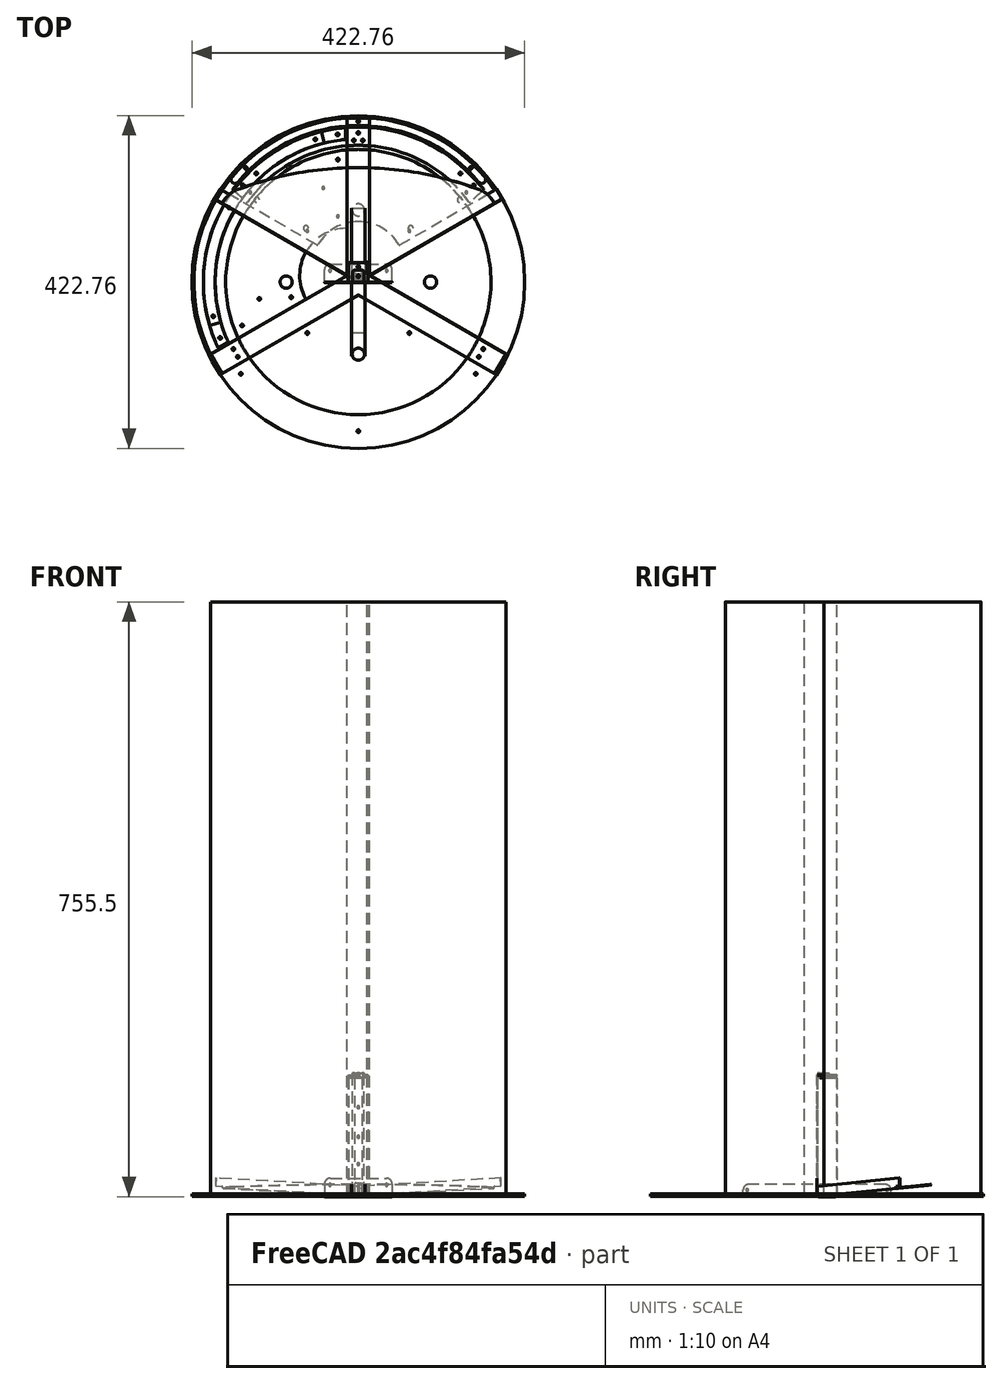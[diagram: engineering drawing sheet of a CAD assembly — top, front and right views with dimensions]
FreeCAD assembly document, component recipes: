
FREECAD ASSEMBLY — COMPONENT RECIPES ("composit_stand3-small")

This assembly document has 17 components, labeled P0..P16 below (a component is one placed body or linked part). 17 of them carry a construction recipe — the FreeCAD feature program that regenerates the part from scratch, quoted from this document or its linked companion documents; the rest are supplied as boundary geometry only. No exploded tour is included for this assembly.
NOTE — document 2 of 2 of this assembly tour. The two overview renders and the header above are repeated from document 1; the component sections below continue where the previous document stopped.
COMPONENT P16 — recipe-attached ("tech_pillar_material_0.50ansi", modeled in this document).
Construction recipe (the document's own serialized feature program — sketch geometry with constraints, then the solid features built on it; lengths are millimeters unless a unit is written):

FEATURE [PartDesign::CoordinateSystem] LCS_0006
  AttacherType = Attacher::AttachEngine3D
  MapMode = 2
  Support = -> [X_Axis037]
FEATURE [Sketcher::SketchObject] Sketch116
  FullyConstrained = true
  MapMode = 5
  Placement = pos=(0,0,0) rot=(0.57735,0.57735,0.57735;2.0944rad)
  Support = -> [YZ_Plane037]
  sketch-geometry (4):
    g0: LineSegment StartX=0 StartY=0 StartZ=0 EndX=25 EndY=0 EndZ=0
    g1: LineSegment StartX=25 StartY=0 StartZ=0 EndX=25 EndY=154 EndZ=0
    g2: LineSegment StartX=25 StartY=154 StartZ=0 EndX=0 EndY=154 EndZ=0
    g3: LineSegment StartX=0 StartY=154 StartZ=0 EndX=0 EndY=0 EndZ=0
  constraints (11):
    c: Coincident(g0,g1)
    c: Coincident(g1,g2)
    c: Coincident(g2,g3)
    c: Coincident(g3,g0)
    c: Horizontal(g0)
    c: Horizontal(g2)
    c: Vertical(g1)
    c: Vertical(g3)
    c: Coincident(g0,g-1)
    c: Distance(g3) = 154  'height'
    c: DistanceX(g0) = 25  'length'
FEATURE [PartDesign::FeaturePython] BaseBend008  # WARN: FeaturePython — macro-defined, semantics opaque (R4)
  BendSide = 1
  BendSketch = -> Sketch116
  MidPlane = true
  Reverse = false
  length = 25
  radius = 0.01
  thickness = 0.3
FEATURE [PartDesign::FeaturePython] Bend015  # WARN: FeaturePython — macro-defined, semantics opaque (R4)
  AutoMiter = true
  BaseFeature = -> BaseBend008
  BendType = 0
  LengthList = [25]
  LengthSpec = 1
  ReliefFactor = 0.7
  UseReliefFactor = false
  angle = 90
  baseObject = -> BaseBend008 [Edge26]
  bendAList = [90]
  extend1 = 0
  extend2 = 0
  gap1 = 3
  gap2 = 3
  invert = false
  kfactor = 0.5
  length = 25
  maxExtendDist = 5
  minGap = 0.1
  minReliefGap = 1
  miterangle1 = 0
  miterangle2 = 0
  offset = 0
  radius = 0.01
  reliefType = 0
  reliefd = 0.1
  reliefw = 0.1
  sketchflip = false
  sketchinvert = false
  unfold = false
FEATURE [PartDesign::FeaturePython] Bend016  # WARN: FeaturePython — macro-defined, semantics opaque (R4)
  AutoMiter = true
  BaseFeature = -> Bend015
  BendType = 0
  LengthList = [25]
  LengthSpec = 0
  ReliefFactor = 0.7
  UseReliefFactor = false
  angle = 90
  baseObject = -> Bend015 [Edge3]
  bendAList = [90]
  extend1 = 0
  extend2 = 0
  gap1 = 3
  gap2 = 0
  invert = false
  kfactor = 0.5
  length = 25
  maxExtendDist = 5
  minGap = 0.1
  minReliefGap = 1
  miterangle1 = 0
  miterangle2 = 0
  offset = 0
  radius = 0.01
  reliefType = 0
  reliefd = 0.1
  reliefw = 0.1
  sketchflip = false
  sketchinvert = false
  unfold = false
FEATURE [PartDesign::FeaturePython] Bend017  # WARN: FeaturePython — macro-defined, semantics opaque (R4)
  AutoMiter = true
  BaseFeature = -> Bend016
  BendType = 0
  LengthList = [25]
  LengthSpec = 0
  ReliefFactor = 0.7
  UseReliefFactor = false
  angle = 90
  baseObject = -> Bend016 [Edge24]
  bendAList = [90]
  extend1 = 0
  extend2 = 0
  gap1 = 0
  gap2 = 3
  invert = false
  kfactor = 0.5
  length = 25
  maxExtendDist = 5
  minGap = 0.1
  minReliefGap = 1
  miterangle1 = 0
  miterangle2 = 0
  offset = 0
  radius = 0.01
  reliefType = 0
  reliefd = 0.1
  reliefw = 0.1
  sketchflip = false
  sketchinvert = false
  unfold = false
FEATURE [Sketcher::SketchObject] Sketch117
  FullyConstrained = true
  MapMode = 5
  Support = -> [XY_Plane038]
  sketch-geometry (5):
    g0: Circle CenterX=0 CenterY=6 CenterZ=0 NormalX=0 NormalY=0 NormalZ=1 AngleXU=0 Radius=1.7
    g1: Circle CenterX=0 CenterY=19 CenterZ=0 NormalX=0 NormalY=0 NormalZ=1 AngleXU=0 Radius=1.7
    g2: LineSegment StartX=0 StartY=0 StartZ=0 EndX=0 EndY=6 EndZ=0
    g3: LineSegment StartX=0 StartY=6 StartZ=0 EndX=0 EndY=19 EndZ=0
    g4: LineSegment StartX=0 StartY=19 StartZ=0 EndX=0 EndY=25 EndZ=0
  constraints (13):
    c: PointOnObject(g0,g-2)
    c: PointOnObject(g1,g-2)
    c: Coincident(g2,g-1)
    c: Coincident(g2,g0)
    c: Coincident(g3,g0)
    c: Coincident(g3,g1)
    c: Coincident(g4,g1)
    c: PointOnObject(g4,g-2)
    c: DistanceY(g4) = 25
    c: Equal(g2,g4)
    c: Distance(g2) = 6
    c: Equal(g0,g1)
    c: Diameter(g0) = 3.4
FEATURE [PartDesign::Pocket] Pocket071
  BaseFeature = -> Bend017
  Direction = (0,0,-1)
  Length = 5
  Length2 = 5
  Midplane = true
  Profile = -> Sketch117
  ReferenceAxis = -> Sketch117 [N_Axis]
  Type = 1
FEATURE [Sketcher::SketchObject] Sketch118
  FullyConstrained = true
  MapMode = 5
  Placement = pos=(0,0,0) rot=(0.57735,0.57735,0.57735;2.0944rad)
  Support = -> [YZ_Plane037]
  sketch-geometry (4):
    g0: LineSegment StartX=60 StartY=130 StartZ=0 EndX=160 EndY=130 EndZ=0
    g1: LineSegment StartX=160 StartY=130 StartZ=0 EndX=160 EndY=180 EndZ=0
    g2: LineSegment StartX=160 StartY=180 StartZ=0 EndX=60 EndY=180 EndZ=0
    g3: LineSegment StartX=60 StartY=180 StartZ=0 EndX=60 EndY=130 EndZ=0
  constraints (12):
    c: Coincident(g0,g1)
    c: Coincident(g1,g2)
    c: Coincident(g2,g3)
    c: Coincident(g3,g0)
    c: Horizontal(g0)
    c: Horizontal(g2)
    c: Vertical(g1)
    c: Vertical(g3)
    c: DistanceY(g3,g3) = 50  'height'
    c: DistanceX(g0,g0) = 100  'length'
    c: DistanceX(g0) = 60
    c: DistanceY(g0) = 130
FEATURE [Sketcher::SketchObject] Sketch126
  FullyConstrained = true
  MapMode = 5
  Support = -> [XY_Plane038]
  sketch-geometry (3):
    g0: LineSegment StartX=12.5 StartY=25 StartZ=0 EndX=12.5 EndY=17.5 EndZ=0
    g1: LineSegment StartX=12.5 StartY=25 StartZ=0 EndX=5 EndY=25 EndZ=0
    g2: ArcOfCircle CenterX=5 CenterY=17.5 CenterZ=0 NormalX=0 NormalY=0 NormalZ=1 AngleXU=0 Radius=7.5 StartAngle=0 EndAngle=1.5708
  constraints (8):
    c: Vertical(g0)
    c: DistanceX(g0) = 12.5
    c: DistanceY(g0) = 25
    c: Coincident(g1,g0)
    c: Horizontal(g1)
    c: Tangent(g2,g0) = 1.5708
    c: Tangent(g2,g1) = -1.5708
    c: Diameter(g2) = 15
FEATURE [PartDesign::Pocket] Pocket080
  BaseFeature = -> Pocket071
  Direction = (0,0,-1)
  Length = 5
  Length2 = 5
  Midplane = true
  Profile = -> Sketch126
  ReferenceAxis = -> Sketch126 [N_Axis]
  Type = 1
FEATURE [Sketcher::SketchObject] Sketch127
  FullyConstrained = true
  MapMode = 5
  Placement = pos=(0,0,0) rot=(0.57735,0.57735,0.57735;2.0944rad)
  Support = -> [YZ_Plane037]
  sketch-geometry (4):
    g0: LineSegment StartX=71.78 StartY=114.36 StartZ=0 EndX=143.27 EndY=114.36 EndZ=0
    g1: LineSegment StartX=143.27 StartY=114.36 StartZ=0 EndX=143.27 EndY=159.55 EndZ=0
    g2: LineSegment StartX=143.27 StartY=159.55 StartZ=0 EndX=71.78 EndY=159.55 EndZ=0
    g3: LineSegment StartX=71.78 StartY=159.55 StartZ=0 EndX=71.78 EndY=114.36 EndZ=0
  constraints (12):
    c: Coincident(g0,g1)
    c: Coincident(g1,g2)
    c: Coincident(g2,g3)
    c: Coincident(g3,g0)
    c: Horizontal(g0)
    c: Horizontal(g2)
    c: Vertical(g1)
    c: Vertical(g3)
    c: DistanceX(g0) = 71.78  'offset_x'
    c: DistanceY(g0) = 114.36  'offset_y'
    c: DistanceY(g3,g3) = 45.19  'height'
    c: DistanceX(g0,g0) = 71.49  'width'
FEATURE [Sketcher::SketchObject] Sketch133
  FullyConstrained = true
  MapMode = 5
  Placement = pos=(0,0,0) rot=(1,0,0;1.5708rad)
  Support = -> [XZ_Plane037]
  sketch-geometry (4):
    g0: Circle CenterX=0 CenterY=41 CenterZ=0 NormalX=0 NormalY=0 NormalZ=1 AngleXU=0 Radius=1.7
    g1: Circle CenterX=0 CenterY=113 CenterZ=0 NormalX=0 NormalY=0 NormalZ=1 AngleXU=0 Radius=1.7
    g2: GeomPoint X=0 Y=77 Z=0
    g3: GeomPoint X=0 Y=154 Z=0
  constraints (8):
    c: PointOnObject(g0,g-2)
    c: PointOnObject(g1,g-2)
    c: DistanceY(g3) = 154
    c: Symmetric(g3,g-1,g2)
    c: Symmetric(g0,g1,g2)
    c: DistanceY(g0,g1) = 72
    c: Equal(g0,g1)
    c: Diameter(g0) = 3.4
FEATURE [PartDesign::Pocket] Pocket090
  BaseFeature = -> Pocket080
  Direction = (0,1,2e-16)
  Length = 5
  Length2 = 5
  Midplane = true
  Profile = -> Sketch133
  ReferenceAxis = -> Sketch133 [N_Axis]
  Type = 1
FEATURE [PartDesign::Body] tech_pillar  label="tech_pillar_material_0.50ansi"
  Group = -> [LCS_0006,Sketch116,BaseBend008,Bend015,Bend016,Bend017,Sketch117,Pocket071,Sketch118,Sketch126,Pocket080,Sketch127,Sketch133,Pocket090]
  Origin = -> Origin037
  Tip = -> Pocket090
PROVENANCE & LICENSES
A FreeCAD (.FCStd) document from a public repository crawl; recipes are the document's own serialized feature recipes (and, for linked parts, companion documents' recipes).
License: as declared in the source repository (recorded in the dataset sidecar).
